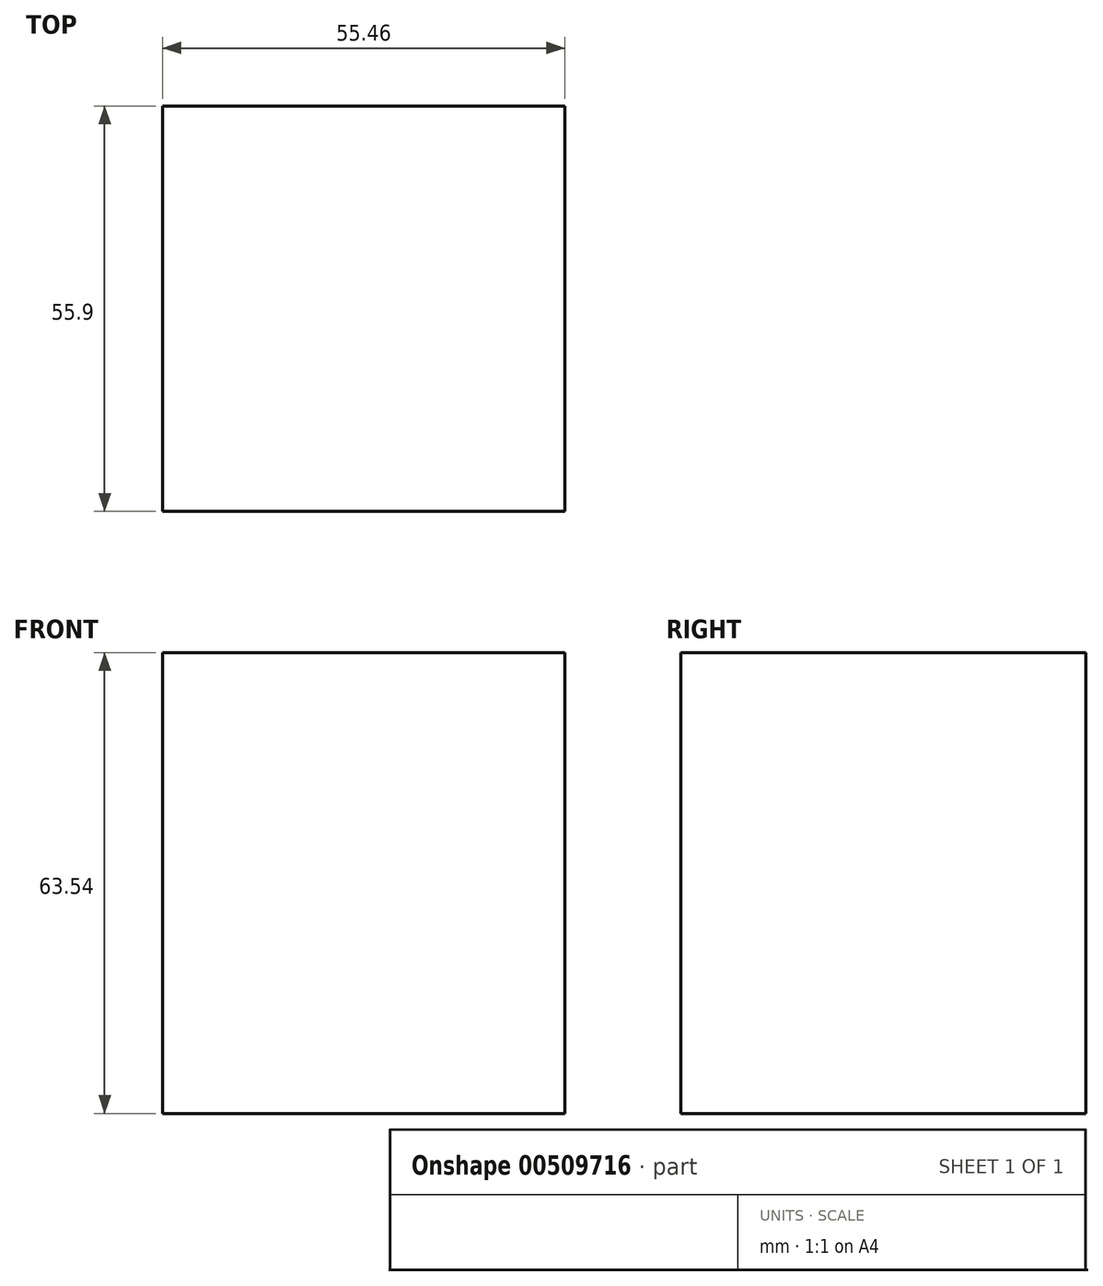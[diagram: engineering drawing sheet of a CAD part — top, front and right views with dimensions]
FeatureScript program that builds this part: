
annotation { "Feature Type Name" : "Feature", "Feature Type Description" : "" }
export const myFeature = defineFeature(function(context is Context, id is Id, definition is map)
    precondition{}
    {
        {
            var Q0;
            Q0=qCreatedBy(makeId("Front.planeOp"),FACE);
            var sketch = newSketch(context, id + "F0", { "sketchPlane" : qUnion([Q0])});
            skLineSegment(sketch, "E0.bottom", {"start": v(-55.46, 63.54) * mm, "end": v(0, 63.54) * mm});
            skLineSegment(sketch, "E0.top", {"start": v(-55.46, 0) * mm, "end": v(0, 0) * mm});
            skLineSegment(sketch, "E0.left", {"start": v(-55.46, 63.54) * mm, "end": v(-55.46, 0) * mm});
            skLineSegment(sketch, "E0.right", {"start": v(0, 63.54) * mm, "end": v(0, 0) * mm});
            skSolve(sketch);
        }
        {
            var Q0;
            Q0 = qSketchRegion(id + "F0", true);
            extrude(context, id + "F1", {"entities" : qUnion([Q0]), "depth" : 55.9 * mm, "offsetDistance" : 25 * mm});
        }
    });
